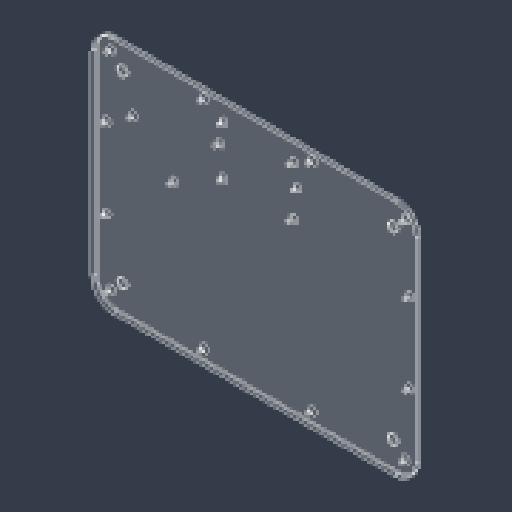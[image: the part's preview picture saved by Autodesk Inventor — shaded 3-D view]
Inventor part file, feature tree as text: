
AUTODESK INVENTOR PART (.ipt)
format: ipt  version: 2023.4 (Build 274418000, 418)  size: 188,416 bytes
history: native  units: mm
features: sketch x6, hole x5, mirror x2, extrude x1, fillet x1, chamfer x1
ambient origin geometry x8: Origin, YZ Plane, XZ Plane, XY Plane, X Axis, Y Axis, Z Axis, Center Point
bodies: Solid1 (feature_tree)
feature tree (16):
  extrude  "Extrusion1"  Depth=220.0mm
  fillet  "Fillet2"  [1 undecoded]
  chamfer  "Chamfer1"  Distance=2.0mm Angle=45.0deg
  hole  "Hole4"  [1 undecoded]
  mirror  "Mirror1"
  mirror  "Mirror2"
  hole  "Hole5"  [1 undecoded]
  hole  "Hole6"  [1 undecoded]
  hole  "Hole7"  [1 undecoded]
  hole  "Hole8"  [1 undecoded]
  sketch  "Sketch1"  dims[d0=300.0mm d1=220.0mm d3=0.0mm]
  sketch  "Sketch8"  dims[d81=20.0mm d82=1.0mm d83=2.0mm d84=45.0deg]
  sketch  "Sketch9"  dims[d93=3.4mm d94=6.0mm d95=7.5mm d96=3.4mm d97=90.0deg d98=8.0mm d99=20.594885mm d100=14.0mm]
  sketch  "Sketch10"  dims[d101=14.0mm d102=10.0mm]
  sketch  "Sketch11"  dims[d103=10.0mm d104=100.0mm]
  sketch  "Sketch12"  dims[d105=73.0mm d106=25.0mm d107=25.0mm d108=9.0mm d109=6.0mm d110=7.5mm d111=2.0mm d112=90.0deg d113=2.0mm d114=0.0mm d115=71.2mm d116=71.4mm d117=3.4mm d118=6.0mm d119=7.5mm d120=2.9mm d121=90.0deg d122=8.0mm d123=20.594885mm d124=50.5mm d127=3.4mm d128=6.0mm d129=7.5mm d130=2.0mm d131=90.0deg d132=8.0mm d133=20.594885mm d134=15.197537mm d135=88.0mm d136=45.0deg d137=45.0mm d138=45.0mm d139=65.0mm d140=3.4mm d141=6.0mm d142=7.5mm d143=2.0mm d144=90.0deg d145=8.0mm d146=20.594885mm]
note: 6 required parameter values undecoded (feature->parameter linkage not recoverable at this tier; creation-order binding heuristic only, values carry confidence <= 0.55)
